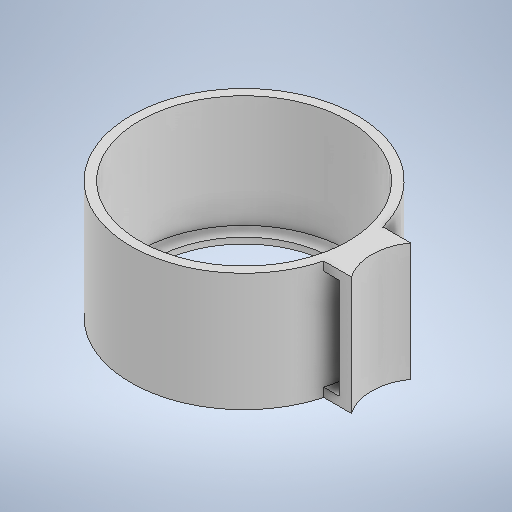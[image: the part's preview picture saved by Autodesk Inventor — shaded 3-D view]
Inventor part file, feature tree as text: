
AUTODESK INVENTOR PART (.ipt)
format: ipt  version: 2025 (Build 290162010, 162A)  size: 321,024 bytes
history: native  units: in
note: dims shown in document units (in); Inventor stores cm internally (conversion verified against a paired STEP export)
features: extrude x5, sketch x5
ambient origin geometry x8: Origin, YZ Plane, XZ Plane, XY Plane, X Axis, Y Axis, Z Axis, Center Point
bodies: Solid1 (feature_tree)
feature tree (10):
  extrude  "Extrusion1"  Depth=3.528in
  extrude  "Extrusion2"  Depth=1.0in TaperAngle=0.0deg
  extrude  "Extrusion3"  Depth=0.1in TaperAngle=0.0deg
  sketch  "Sketch4"  dims[d10=1.0in d11=0.0in d12=1.0in d13=0.0in]
  extrude  "Extrusion4"  Depth=1.0in TaperAngle=0.0deg
  extrude  "Extrusion5"  [1 undecoded]
  sketch  "Sketch1"  dims[d0=3.828in d1=3.528in]
  sketch  "Sketch2"  dims[d2=2.0in d3=0.0in d5=1.0in d6=0.0in]
  sketch  "Sketch3"  dims[d7=3.04in d8=0.1in d9=0.0in]
  sketch  "Sketch5"
note: 1 required parameter value undecoded (feature->parameter linkage not recoverable at this tier; creation-order binding heuristic only, values carry confidence <= 0.55)
